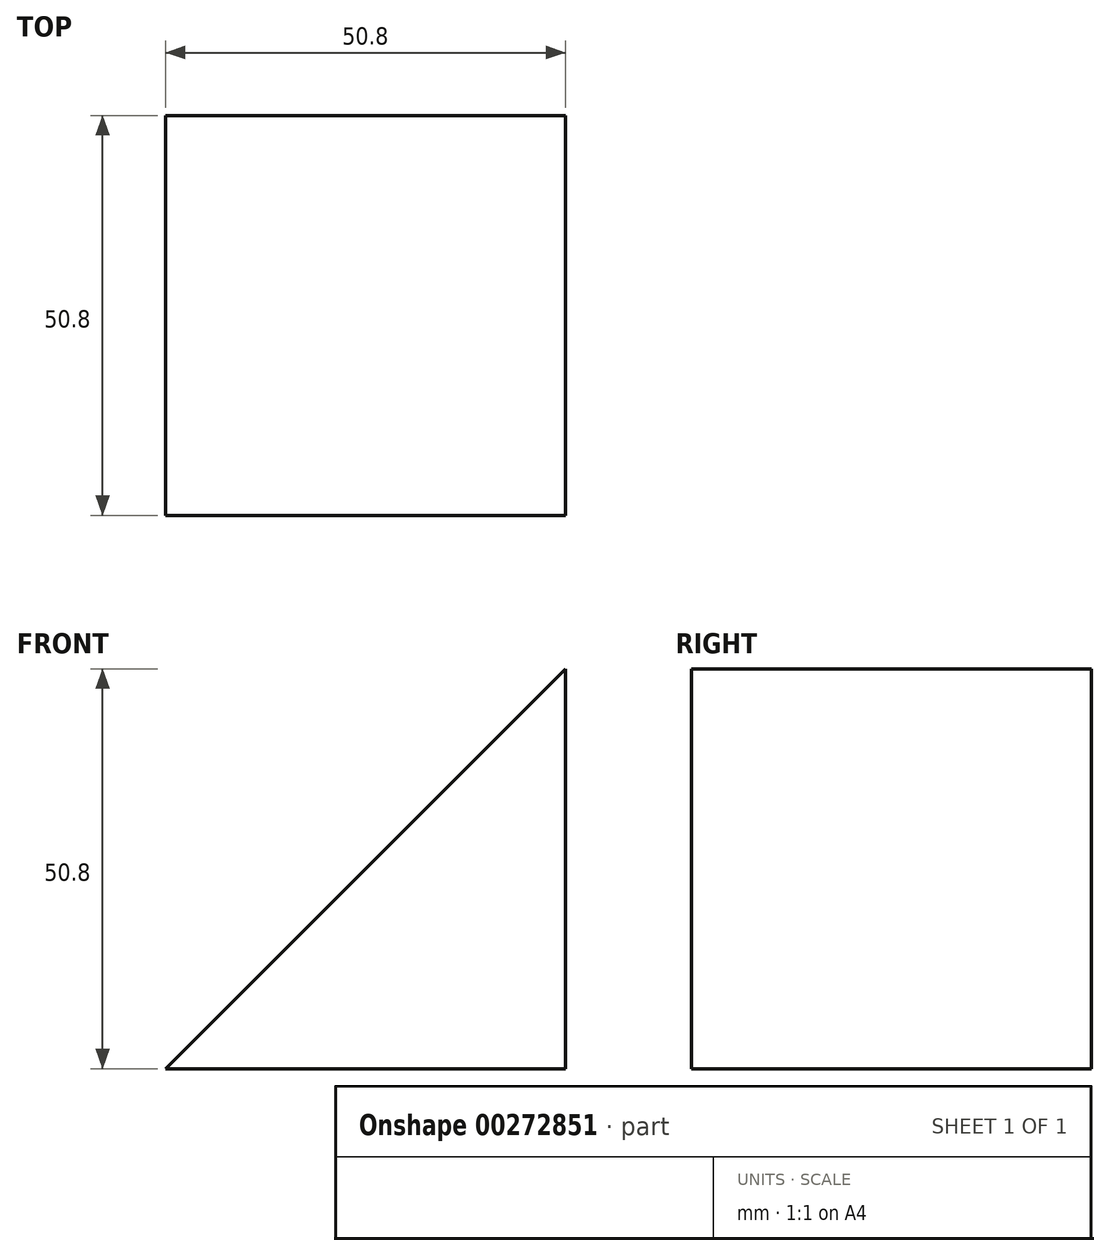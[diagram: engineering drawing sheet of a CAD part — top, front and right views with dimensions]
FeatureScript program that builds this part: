
annotation { "Feature Type Name" : "Feature", "Feature Type Description" : "" }
export const myFeature = defineFeature(function(context is Context, id is Id, definition is map)
    precondition{}
    {
        {
            var Q0;
            Q0=qCreatedBy(makeId("Front.planeOp"),FACE);
            var sketch = newSketch(context, id + "F0", { "sketchPlane" : qUnion([Q0])});
            skLineSegment(sketch, "E0", {"start": v(0, 0) * mm, "end": v(0, 50.8) * mm});
            skLineSegment(sketch, "E1", {"start": v(0, 0) * mm, "end": v(-50.8, 0) * mm});
            skLineSegment(sketch, "E2", {"start": v(-50.8, 0) * mm, "end": v(0, 50.8) * mm});
            skSolve(sketch);
        }
        {
            var Q0;
            Q0 = qSketchRegion(id + "F0", true);
            extrude(context, id + "F1", {"entities" : qUnion([Q0]), "depth" : 50.8 * mm});
        }
    });
